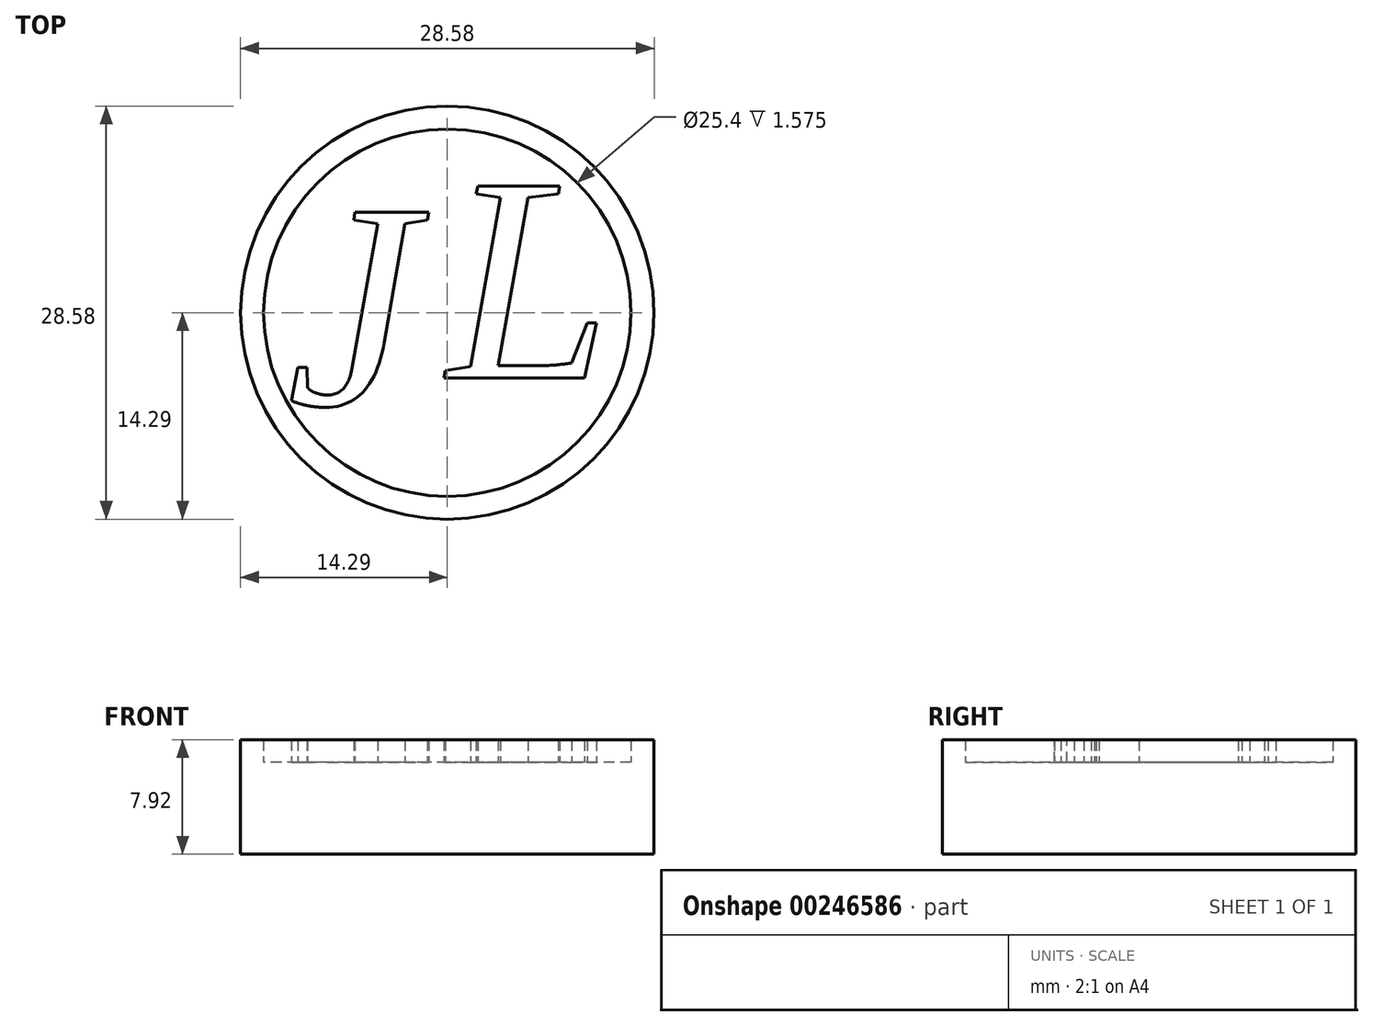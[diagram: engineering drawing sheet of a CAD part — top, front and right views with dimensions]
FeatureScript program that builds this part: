
annotation { "Feature Type Name" : "Feature", "Feature Type Description" : "" }
export const myFeature = defineFeature(function(context is Context, id is Id, definition is map)
    precondition{}
    {
        {
            var Q0;
            Q0=qCreatedBy(makeId("Top.planeOp"),FACE);
            var sketch = newSketch(context, id + "F0", { "sketchPlane" : qUnion([Q0])});
            skCircle(sketch, "E0", {"center": v(0, 0) * mm, "radius": 14.29 * mm});
            skSolve(sketch);
        }
        {
            var Q0;
            Q0=makeQuery(id+"F0.imprint","IMPRINT",FACE,{"disambiguationData":[TD([[makeQuery(id+"F0.imprint","IMPRINT",EDGE,{"derivedFrom":sQuery(id+"F0.wireOp",EDGE,"E0")}),1.0]])]});
            extrude(context, id + "F1", {"entities" : qUnion([Q0]), "depth" : 6.35 * mm});
        }
        {
            var Q0;
            Q0=makeQuery(id+"F1.opExtrude","CAP_FACE",FACE,{"disambiguationData":[OSD([sQuery(id+"F0.wireOp",EDGE,"E0")])],"isStart":false});
            var sketch = newSketch(context, id + "F2", { "sketchPlane" : qUnion([Q0])});
            skCircle(sketch, "E1", {"center": v(0, 0) * mm, "radius": 12.7 * mm});
            skSolve(sketch);
        }
        {
            var Q0;
            Q0=makeQuery(id+"F2.imprint","IMPRINT",FACE,{"disambiguationData":[TD([[makeQuery(id+"F2.imprint","IMPRINT",EDGE,{"derivedFrom":sQuery(id+"F2.wireOp",EDGE,"E1")}),-1.0]])]});
            extrude(context, id + "F3", {"entities" : qUnion([Q0]), "operationType" : NewBodyOperationType.ADD, "depth" : 1.57 * mm});
        }
        {
            var Q0;
            Q0=makeQuery(id+"F1.opExtrude","CAP_FACE",FACE,{"disambiguationData":[OSD([sQuery(id+"F0.wireOp",EDGE,"E0")])],"isStart":false});
            var sketch = newSketch(context, id + "F4", { "sketchPlane" : qUnion([Q0])});
            skText(sketch, "E2", { "text": "J", "fontName": "Tinos-Italic.ttf"});
            skText(sketch, "E3", { "text": "L", "fontName": "Tinos-Italic.ttf"});
            const initialGuessF4  = {"E2": [-0.01107, -0.00635, 1, 0, 0.0146], "E3": [0, -0.00453, 1, 0, 0.0146]};
            skSetInitialGuess(sketch, initialGuessF4);
            skSolve(sketch);
        }
        {
            var Q0;
            Q0=makeQuery(id+"F4.imprint","IMPRINT",FACE,{"disambiguationData":[TD([[makeQuery(id+"F4.imprint","IMPRINT",EDGE,{"derivedFrom":sQuery(id+"F4.wireOp",EDGE,"E2.sketch_text.stroke-0")}),-1.0]])]});
            extrude(context, id + "F5", {"entities" : qUnion([Q0]), "operationType" : NewBodyOperationType.ADD, "depth" : 1.57 * mm});
        }
        {
            var Q0;
            Q0=makeQuery(id+"F4.imprint","IMPRINT",FACE,{"disambiguationData":[TD([[makeQuery(id+"F4.imprint","IMPRINT",EDGE,{"derivedFrom":sQuery(id+"F4.wireOp",EDGE,"E3.sketch_text.stroke-0")}),-1.0]])]});
            extrude(context, id + "F6", {"entities" : qUnion([Q0]), "operationType" : NewBodyOperationType.ADD, "depth" : 1.57 * mm});
        }
    });
